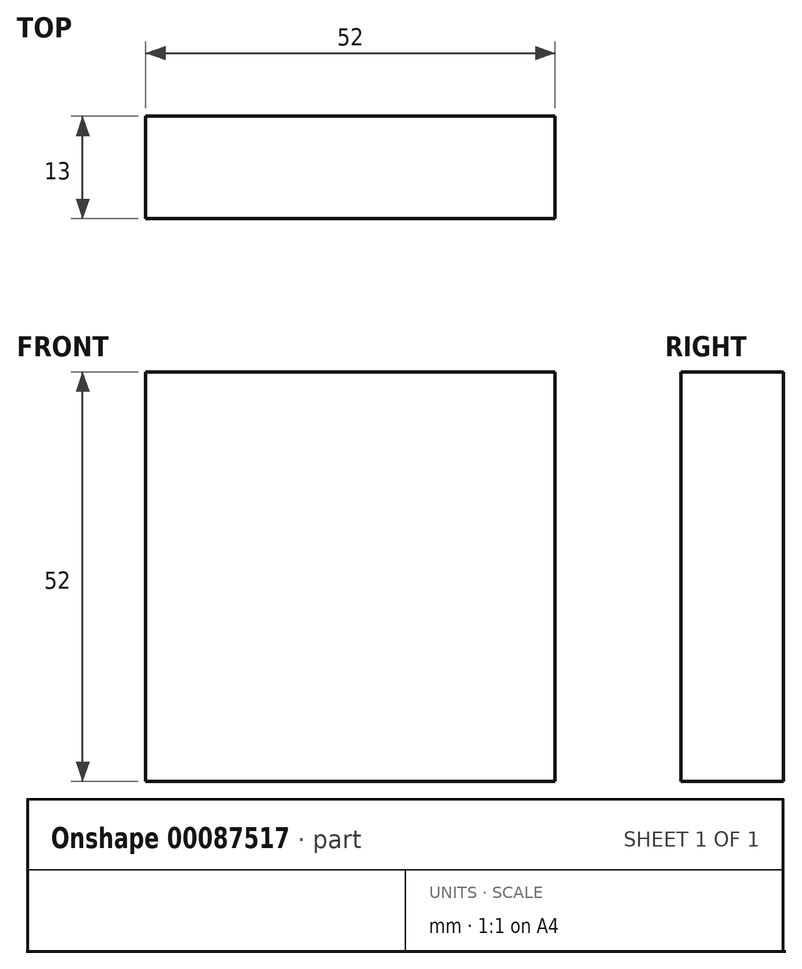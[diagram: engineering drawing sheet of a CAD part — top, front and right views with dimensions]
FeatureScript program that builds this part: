
annotation { "Feature Type Name" : "Feature", "Feature Type Description" : "" }
export const myFeature = defineFeature(function(context is Context, id is Id, definition is map)
    precondition{}
    {
        {
            var Q0;
            Q0=qCreatedBy(makeId("Front.planeOp"),FACE);
            var sketch = newSketch(context, id + "F0", { "sketchPlane" : qUnion([Q0])});
            skLineSegment(sketch, "E0.bottom", {"start": v(26, -26) * mm, "end": v(-26, -26) * mm});
            skLineSegment(sketch, "E0.top", {"start": v(26, 26) * mm, "end": v(-26, 26) * mm});
            skLineSegment(sketch, "E0.left", {"start": v(26, -26) * mm, "end": v(26, 26) * mm});
            skLineSegment(sketch, "E0.right", {"start": v(-26, -26) * mm, "end": v(-26, 26) * mm});
            skPoint(sketch, "E0.middle", {"position": v(0, 0) * mm});
            skSolve(sketch);
        }
        {
            var Q0;
            Q0 = qSketchRegion(id + "F0", true);
            extrude(context, id + "F1", {"entities" : qUnion([Q0]), "endBound" : BoundingType.SYMMETRIC, "depth" : 13 * mm});
        }
    });
